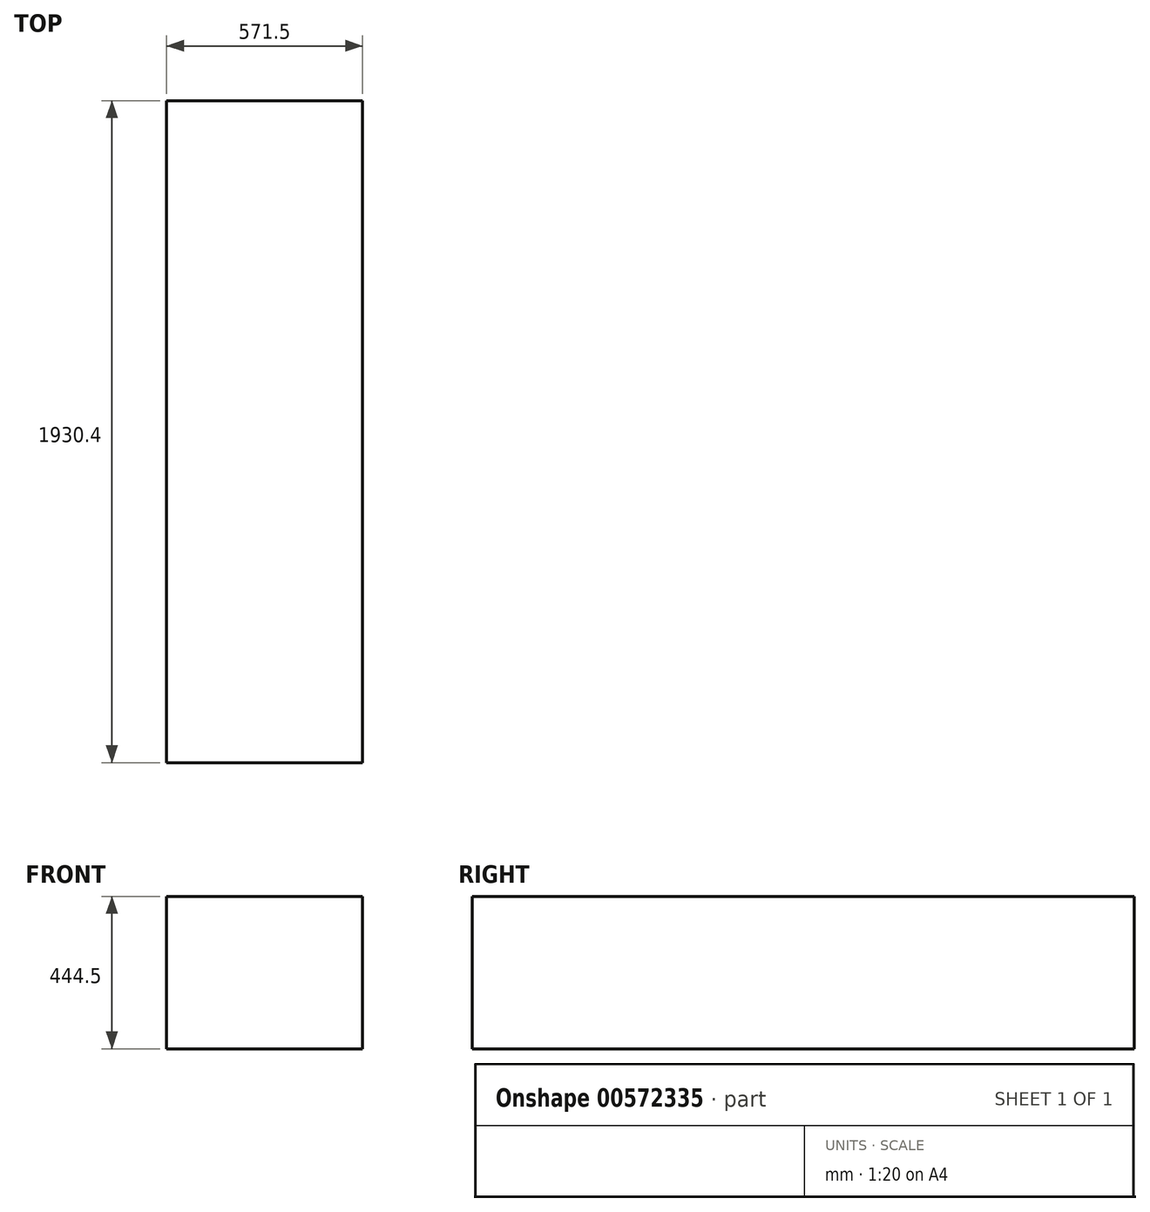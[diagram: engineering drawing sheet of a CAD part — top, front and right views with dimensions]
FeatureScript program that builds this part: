
annotation { "Feature Type Name" : "Feature", "Feature Type Description" : "" }
export const myFeature = defineFeature(function(context is Context, id is Id, definition is map)
    precondition{}
    {
        {
            var Q0;
            Q0=qCreatedBy(makeId("Top.planeOp"),FACE);
            var sketch = newSketch(context, id + "F0", { "sketchPlane" : qUnion([Q0])});
            skLineSegment(sketch, "E0.bottom", {"start": v(0, 0) * mm, "end": v(-571.5, 0) * mm});
            skLineSegment(sketch, "E0.top", {"start": v(0, 1930.4) * mm, "end": v(-571.5, 1930.4) * mm});
            skLineSegment(sketch, "E0.left", {"start": v(0, 0) * mm, "end": v(0, 1930.4) * mm});
            skLineSegment(sketch, "E0.right", {"start": v(-571.5, 0) * mm, "end": v(-571.5, 1930.4) * mm});
            skSolve(sketch);
        }
        {
            var Q0;
            Q0 = qSketchRegion(id + "F0", true);
            extrude(context, id + "F1", {"entities" : qUnion([Q0]), "depth" : 444.5 * mm, "offsetDistance" : 25.4 * mm});
        }
    });
